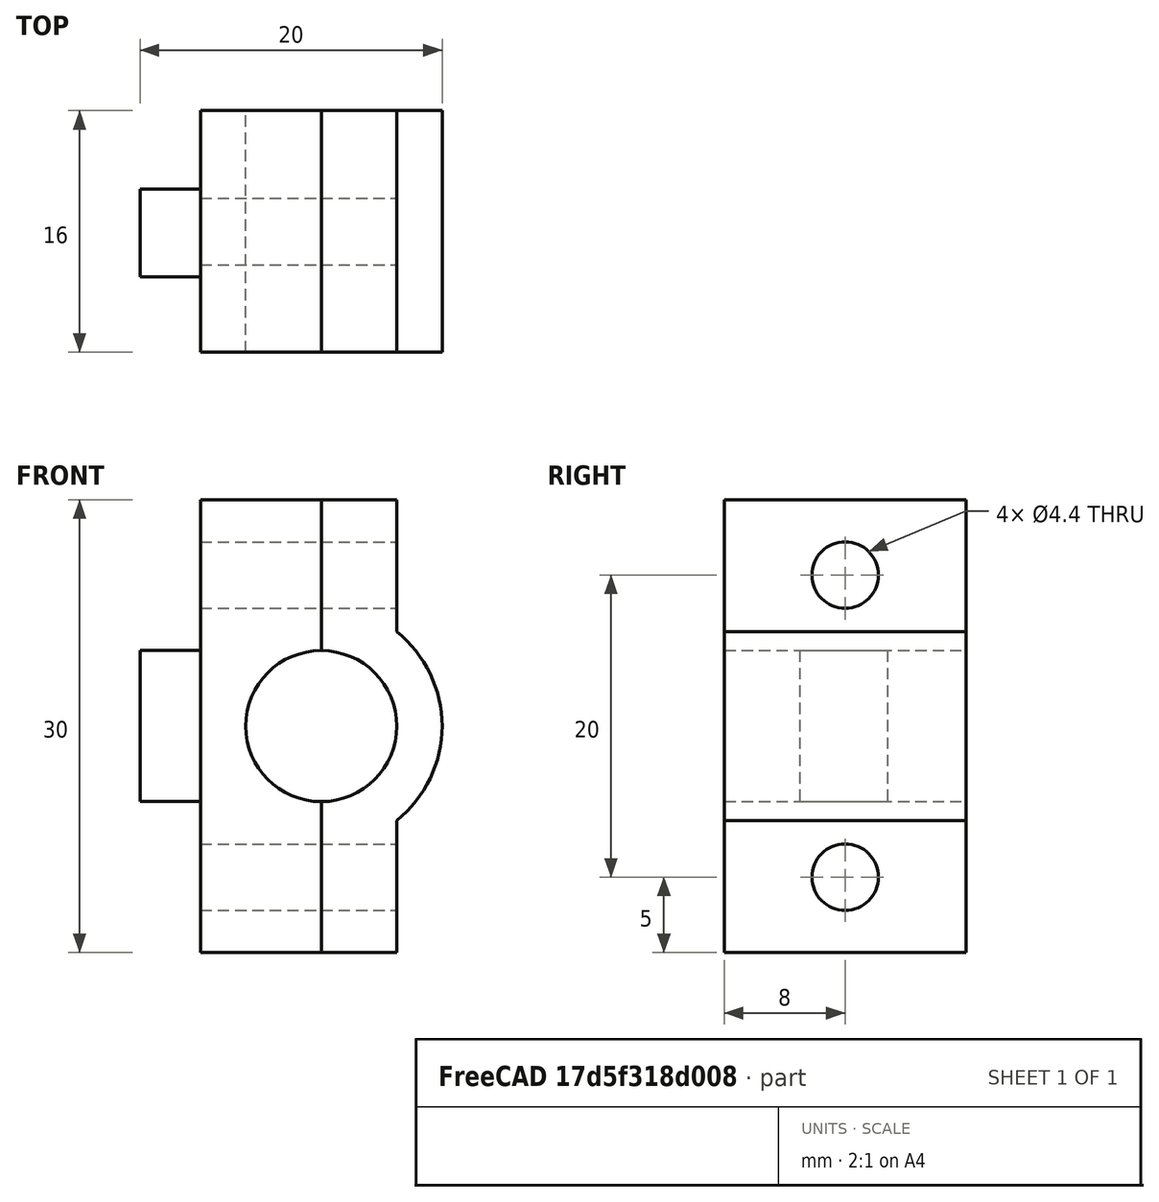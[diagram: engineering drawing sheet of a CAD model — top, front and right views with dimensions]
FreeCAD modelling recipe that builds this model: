
FCSTD DOCUMENT  (FreeCAD 0.18R16110 (Git))
Label: y-mount-4x
License: All rights reserved
LicenseURL: http://en.wikipedia.org/wiki/All_rights_reserved
objects: Part::Cylinder×7, Part::Cut×6, Part::Box×3, Part::MultiFuse×2, Mesh::Feature×2, Spreadsheet::Sheet×1
note: 18 computed .brp shape members not serialized (recipe doc carries the construction recipe); baked Part::Feature solids carry a one-line shape summary decoded from their .brp

FEATURE [Part::Cylinder] Cylinder066  label="Zylinder055"
  Angle = 360
  AttacherType = Attacher::AttachEngine3D
  Height = 20
  Placement = pos=(-10,9,8) rot=(1,0,0;1.5708rad)
  Radius = 2.2
FEATURE [Part::Box] Box052  label="Quader031"
  AttacherType = Attacher::AttachEngine3D
  Height = 16
  Length = 30
  Placement = pos=(-15,-5,0) rot=(0,0,1;0rad)
  Width = 5
FEATURE [Part::Cylinder] Cylinder065  label="Zylinder054"
  Angle = 180
  AttacherType = Attacher::AttachEngine3D
  Height = 16
  Placement = pos=(0,0,0) rot=(0,0,1;3.14159rad)
  Radius = 8
FEATURE [Part::Cylinder] Cylinder068  label="Zylinder057"
  Angle = 360
  AttacherType = Attacher::AttachEngine3D
  Height = 16
  Radius = 5
FEATURE [Part::Cylinder] Cylinder067  label="Zylinder056"
  Angle = 360
  AttacherType = Attacher::AttachEngine3D
  Height = 20
  Placement = pos=(10,9,8) rot=(1,0,0;1.5708rad)
  Radius = 2.2
FEATURE [Part::Box] Box051  label="Quader030"
  AttacherType = Attacher::AttachEngine3D
  Height = 16
  Length = 30
  Placement = pos=(-15,0,0) rot=(0,0,1;0rad)
  Width = 8
FEATURE [Part::Cylinder] Cylinder064  label="Zylinder053"
  Angle = 360
  AttacherType = Attacher::AttachEngine3D
  Height = 16
  Radius = 5
FEATURE [Part::MultiFuse] Fusion035
  Shapes = -> [Box052,Cylinder065]
FEATURE [Part::Cut] Cut072
  Base = -> Fusion035
  Tool = -> Cylinder068
FEATURE [Part::Cut] Cut071
  Base = -> Box051
  Tool = -> Cylinder064
FEATURE [Part::Cut] Cut073
  Base = -> Cut071
  Tool = -> Cylinder067
FEATURE [Part::Cut] Cut074
  Base = -> Cut073
  Tool = -> Cylinder066
FEATURE [Part::Box] Box053  label="Quader032"
  AttacherType = Attacher::AttachEngine3D
  Height = 5.8
  Length = 10
  Placement = pos=(-5,8,5) rot=(0,0,1;0rad)
  Width = 4
  expr: Placement.Base.z = 8 - 3
FEATURE [Part::MultiFuse] Fusion036  label="y_mount_bottom"
  Placement = pos=(-9.75,-14.15,29.85) rot=(0.57735,-0.57735,-0.57735;4.18879rad)
  Shapes = -> [Cut074,Box053]
  expr: Placement.Base.y = Spreadsheet.E27 - 8 - 10
  expr: Placement.Base.x = -Spreadsheet.x_dlinear / 2
  expr: Placement.Base.z = Spreadsheet.x_dlinear / 2 + Spreadsheet.tolerance / 2 + Spreadsheet.x_df + Spreadsheet.y_swand * 2
FEATURE [Part::Cylinder] Cylinder070  label="Zylinder059"
  Angle = 360
  AttacherType = Attacher::AttachEngine3D
  Height = 20
  Placement = pos=(10,9,8) rot=(1,0,0;1.5708rad)
  Radius = 2.2
FEATURE [Part::Cylinder] Cylinder069  label="Zylinder058"
  Angle = 360
  AttacherType = Attacher::AttachEngine3D
  Height = 20
  Placement = pos=(-10,9,8) rot=(1,0,0;1.5708rad)
  Radius = 2.2
FEATURE [Part::Cut] Cut075
  Base = -> Cut072
  Tool = -> Cylinder069
FEATURE [Part::Cut] Cut076  label="y_mount_top"
  Base = -> Cut075
  Placement = pos=(-9.75,-14.15,29.85) rot=(0.57735,-0.57735,-0.57735;4.18879rad)
  Tool = -> Cylinder070
  expr: Placement.Base.y = Spreadsheet.E27 - 8 - 10
  expr: Placement.Base.x = -Spreadsheet.x_dlinear / 2
  expr: Placement.Base.z = Spreadsheet.x_dlinear / 2 + Spreadsheet.tolerance / 2 + Spreadsheet.x_df + Spreadsheet.y_swand * 2
FEATURE [Spreadsheet::Sheet] Spreadsheet
  cells = A1=Toleranz; B1(tolerance)=0.2; D1=x_pos; E1=0; G1=y_pos; H1=0; A2=z_pos; B2=-10; E2=min 0 / max 297; G2=min y_pos; H2=94; I2=max 560; A3=Z-Support; D3=X-Support; G3=y-Support; J3=structure; A4=Führung d; B4(z_df)=8; D4=Führung d; E4(x_df)=10; G4=Führung d; H4(y_df)=10; J4=profil B; K4=20; A5=Führung l; B5(z_fl)==Spreadsheet.z_hub + Spreadsheet.z_hmount * 2 + Spreadsheet.z_hs - 5; D5=Führung l; E5(x_lf)=420; F5=400; G5=Führung l; H5(y_fl)=700; I5=500; J5=distanz Führung; K5=3; A6=Abstand Führung z_sfa; B6(z_sfa)==(z_dlinear + 2 * z_swand + 2 * z_sriemenspiel + z_lriemen) * 1 + (2 * x_hlinear + +z_swand - z_df + 4 * tolerance) * 0; D6=Abstand Führung x_sfa; E6(x_sfa)=65; G6=Abstand Fü y_sfa; H6(y_sfa)==x_lf - x_dlinear - 2 * y_swand; J6=höhe; K6=300; J7=add to Top; K7=18; A8=Schlittenwand swand; B8(z_swand)=5; D8=Schlitten swand; E8(x_swand)=4; G8=y_swand; H8(y_swand)=5; A9=Schlittenlänge z_ls; B9(z_ls)==z_sfa + z_dlinear; D9=Schlittenlänge; E9(x_ls)==z_lmount; A10=Schlittenbreite z_bs; B10(z_bs)==2 * z_swand + z_dlinear; D10=Schlitten breite; E10(x_bs)==Spreadsheet.x_swand * 2 + Spreadsheet.x_dlinear + Spreadsheet.x_sfa; G10=d Antrieb; H10=5; A11=Schlittenhöhe z_hs; B11(z_hs)==z_hlinear + 2 * z_swand; D11=schlittenhöhe x_hs; E11(x_hs)==x_dlinear + x_swand; A12=Hub; B12(z_hub)=100; A14=Linearlager; A15=durchmesser z_dlinear; B15(z_dlinear)=15.4; D15=durchmesser x_dlinear; E15(x_dlinear)=19.5; A16=höhe z_hlinear; B16(z_hlinear)=24.4; D16=höhe x_hlinear; E16(x_hlinear)=29.4; A18=Riemenscheibe bohrung; B18=5; A19=durchmesser z_driemen; B19(z_driemen)=16; D19=dopper pulley; E19=27.5; F19=15.8; A20=länge z_lriemen; B20(z_lriemen)=28; D20=pulley; E20=15.25; F20=15.8; G20=20 Zähne: 2* 180 °; H20=2mm*20 Zähne; I20==40mm; A21=spiel riemenscheibe z_sriemenspiel; B21(z_sriemenspiel)=2; A22=Bohreung z_dbohrung; B22(z_dbohrung)=8; C22=durchmesser Laufbuchse; D22=x_mount; A23=Bohrunlänge z_lbohrung; B23(z_lbohrung)=5; D23=Breite x_mount; E23==y_swand + x_dlinear; A24=riemenbreite z_briemen; B24(z_briemen)=6; D24=Länge x_mount; E24==x_sfa + x_df + y_swand * 2; A25=pitch z_rriemenpitch; B25(z_rriemepitch)=7; D25=Höhe x_mount; E25==y_swand * 2 + x_df + +y_swand + x_dlinear + y_swand; A26=achsen pos y; B26==-Spreadsheet.z_driemen / 2 - Spreadsheet.tolerance * 2; D26= xpos; E26==-Spreadsheet.E23; A27=achsen pos z; B27==(Spreadsheet.z_hub + Spreadsheet.z_hs + Spreadsheet.x_hs) / 2 + z_hmount - z_dbohrung / 2 - Spreadsheet.z_dbohrung / 2; D27=ypos; E27==Spreadsheet.x_swand + Spreadsheet.x_dlinear / 2 + Spreadsheet.tolerance / 2 - Spreadsheet.x_df / 2 - Spreadsheet.y_swand; D28= zpos; E28==-y_swand; A29=Mount; A30=Höhe mount; B30(z_hmount)=20; A31=Länge mount; B31(z_lmount)==z_swand * 2 + z_df + z_sfa; A32=Breite mount; B32(z_bmount)==(Spreadsheet.z_swand + Spreadsheet.z_driemen + Spreadsheet.tolerance * 2) * 0 + 26; A34=Nema; D34=Nema x; A35=Länge; B35(lnema)=42; D35(nema_x_b)=42; A36=Breite; B36(bnema)=42; D36=42; A37=Höhe; B37(hnema)=34; D37(nema_x_h)=48; A38=Achslänge; B38(lanema)=20; D38(nema_x_al)=22; A39=achsen pos y; B39(nema_achse_y)==sqrt(B43 ^ 2 - (B27 - B40) ^ 2) + B26; E39(nemax_achsey)==Spreadsheet.x_swand + Spreadsheet.x_df / 2 + Spreadsheet.x_dlinear / 2 + Spreadsheet.nema_x_h + 2; A40=achsen pos z; B40(nema_achse_z)==x_hs + lnema / 2 + 4; E40(nema_x_achsez)==-Spreadsheet.x_hs / 2; A41=achsen pos x; B41(nema_achse_x)==(z_lmount - z_lriemen) / 2 - z_sriemenspiel; E41(nema_x_achsex)==Spreadsheet.x_lf - Spreadsheet.nema_x_b / 2 - Spreadsheet.y_df; A42=länge zahnriemen; B42=200; C42=gerechnet; A43=abstand achsen; B43==(B42 - 40) / 2; C43==sqrt((Spreadsheet.B27 - Spreadsheet.nema_achse_z) ^ 2 + (-Spreadsheet.B26 + Spreadsheet.nema_achse_y) ^ 2) * 2 + 2 * pi * 7; D43=Zahnriemen x; D44=Breite; E44=6; A45=doppel pulley; D45=Höhe; E45==(Spreadsheet.F20 + Spreadsheet.tolerance * 2) * 0 + 15; A46= achse1  x pos; B46==z_lmount / 2 - (6.5 + 8.9) / 2; D46=Länge; E46==y_sfa + x_dlinear + y_swand * 2 + 2 + nema_x_b / 2; A47= achse2 xpos; B47==z_lmount / 2 + (6.5 + 8.9) / 2; B48==-atan((Spreadsheet.B27 - Spreadsheet.nema_achse_z) / (-Spreadsheet.B26 + Spreadsheet.nema_achse_y))
FEATURE [Mesh::Feature] Mesh  label="y_mount_bottom (Meshed)"
FEATURE [Mesh::Feature] Mesh001  label="y_mount_top (Meshed)"
